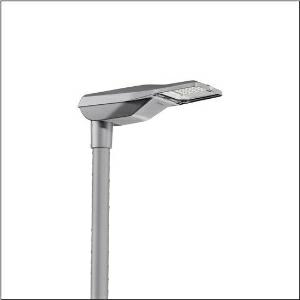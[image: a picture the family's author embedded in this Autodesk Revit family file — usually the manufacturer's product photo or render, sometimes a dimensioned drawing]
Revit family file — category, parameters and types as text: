
# Revit family: streetlight_sl_21_iq_micro___stw1_0a_5xe1e31d08cb_0f3c
name_source: partatom
category: Lighting Fixtures
units: mm (PartAtom-declared; Revit-internal decimal feet)

## family parameters
Cut with Voids When Loaded = No
Host = Face
Light Source = No
Part Type = Normal
Room Calculation Point = No
Round Connector Dimension = Use Diameter
Shared = No

## types (1)
- --- (1 x LED, 2870 lm, 19.4 W, 3000K)
    Apparent Load = 19 VA
    CIE Flux Codes = 38 75 98 100 100
    Color Rendering = 70
    Color Temperature = 3000K
    Default Elevation = 1800 mm
    Description = Streetlight SL 21 iQ micro, mast luminaire, primary light control with lens, of PMMA, primary optical cover: cover, of toughened safety glass, transparent, light distribution: STW1.0a, light emission: direct distribution, primary light characteristic: asymmetric, installation type: post-top, side-entry, LED, High Power LED, rated luminous flux: 2.870lm, luminous efficacy: 148lm/W, light colour: 730, colour temperature: 3000K, control gear: iQ-Comfort, control: Auto-Match, Temp-Guard, Lumen-Switch, Night-Set, Smart-Wire, Light-Fading, Desk-Remote (wireless, voltage-free reading and setting of iQ features in the workshop via application-optimized NFC function/RFID function), optimised constant luminous flux control (CLO 2.0), pre-setting: linear dimming characteristic, mains connection: 220..240V, AC, 50/60Hz, start of lifetime: 19W, end of service life: 20W, reduction: 10W, luminaire housing, of diecast aluminium, powder-coated, SITECO metallic grey (DB 702S), corrosivity category C5 high according to DIN EN ISO 12944, please order mast flange separately, inclination adjustable: 0°, 5°, 10°, 15°, sealing non-destructively replaceable, multi-level sealing system, length: 528mm, width: 235mm, height: 110mm, mast flange for spigot size: 42mm (side-entry): 5XC10008XM4, 60/48mm (side-entry/post-top): 5XC10108XM2, 76/60mm (side-entry/post-top): 5XC10108XM1, protection rating (complete): IP66, insulation class (complete): insulation class II (safety insulation), certification: CE, ENEC, ENEC+, VDE, impact resistance: IK10, permissible operating ambient temperature for outdoor applications: -40..+50°C, standard-compliant lighting for roads and squares, packaging unit: 1 piece

Light Distribution: STW1.0a
    Height = 110 mm
    Lamp = 1 x LED
    Lamp Light Flux = 2870 lm
    Lamp Power = 19.4 W
    Lamp count = 1
    Length = 528 mm
    Luminous efficacy = 148 lm/W
    Manufacturer = Siteco
    ModVariant = No
    Model = 5XE1E31D08CB
    Number of Poles = 1
    OnlyDefault = Yes
    Power Factor = 1
    Product Name = Streetlight SL 21 iQ micro | STW1.0a
    Product group = mast luminaire | pylon top
    ProductGroupID = 6100
    Protection Class = Protection class II
    Protection Degree = IP 66
    RLX_Detail_Level = 1
    RLX_Emergency_Light_Flux = 0 lm
    RLX_Emergency_Type = 0
    RLX_Emergency_Type_DB = No
    RlxData = <blob elided: 98857 chars, md5=9a1ec842>
    Socket = socket
    Standby Power = 0 W
    System Light Flux = 2870 lm
    System Power = 19 W
    Type Comments = factory setting: luminous flux: 100 % | dim-lin: 254 | 387 mA
    Type Image = l_1006881.jpg
    URL = http://relux.com
    VarID = @adj_138391
    Voltage = 0 V
    Weight = 0.00 kg
    Width = 235 mm

## geometry (parser evidence)
native form markers: Blend x4, Sweep x10
no freeform markers — native parametric forms only
